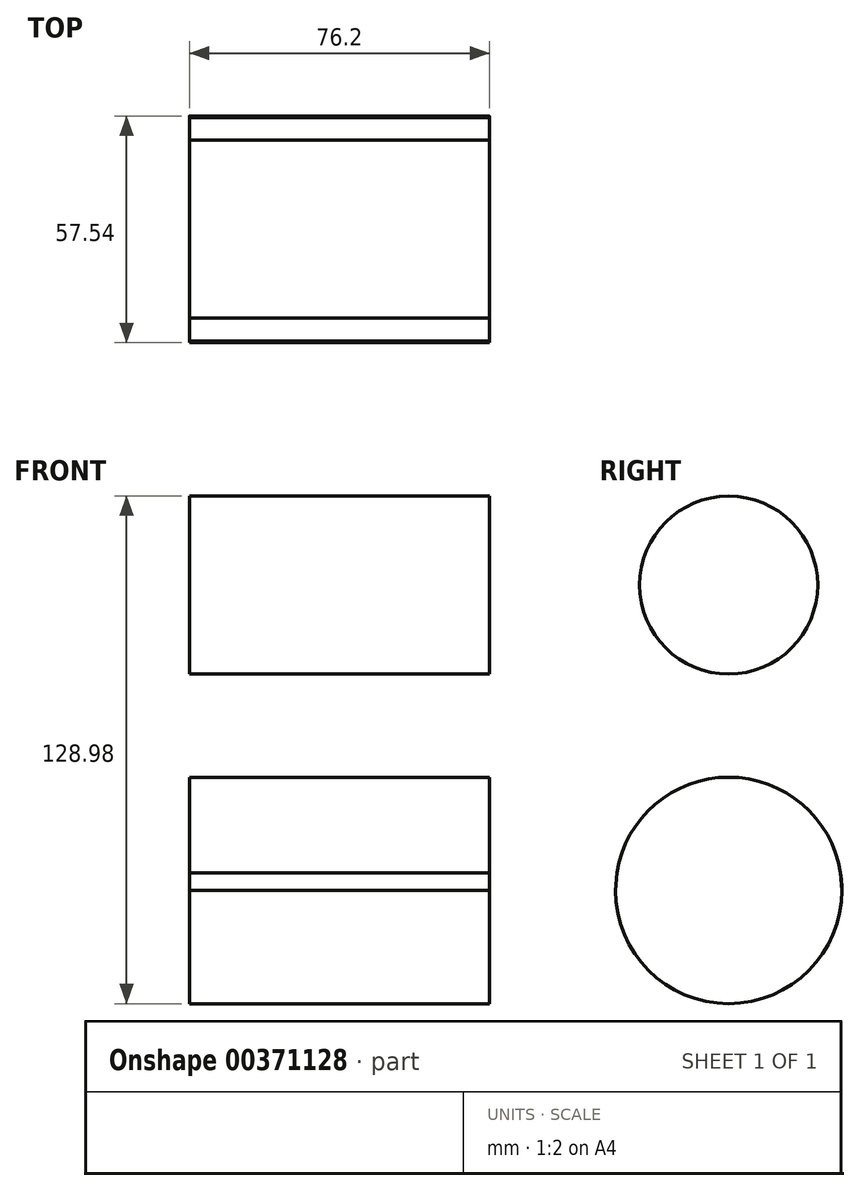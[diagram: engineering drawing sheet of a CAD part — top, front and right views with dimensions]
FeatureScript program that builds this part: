
annotation { "Feature Type Name" : "Feature", "Feature Type Description" : "" }
export const myFeature = defineFeature(function(context is Context, id is Id, definition is map)
    precondition{}
    {
        {
            var Q0;
            Q0=qCreatedBy(makeId("Right.planeOp"),FACE);
            var sketch = newSketch(context, id + "F0", { "sketchPlane" : qUnion([Q0])});
            skCircle(sketch, "E0", {"center": v(0, 0) * mm, "radius": 28.77 * mm});
            skCircle(sketch, "E1", {"center": v(0, 77.59) * mm, "radius": 22.62 * mm});
            skLineSegment(sketch, "E2", {"start": v(-28.77, 0) * mm, "end": v(-22.55, 79.36) * mm});
            skLineSegment(sketch, "E3", {"start": v(28.77, 0) * mm, "end": v(22.55, 79.36) * mm});
            skSolve(sketch);
        }
        {
            var Q0;
            {var subQ0=sQuery(id+"F0.wireOp",EDGE,"E2");var subQ1=sQuery(id+"F0.wireOp",EDGE,"E0");var subQ2=makeQuery(id+"F0.imprint","INTERSECT",VERTEX,{"disambiguationData":[OD(0.0)],"derivedFrom":[subQ1,subQ0]});Q0=makeQuery(id+"F0.imprint","IMPRINT",FACE,{"disambiguationData":[TD([[makeQuery(id+"F0.imprint","IMPRINT",EDGE,{"disambiguationData":[TD([[subQ2,1.0]])],"derivedFrom":subQ1}),1.0]])]});}
            var Q1;
            {var subQ0=sQuery(id+"F0.wireOp",EDGE,"E3");var subQ1=sQuery(id+"F0.wireOp",EDGE,"E0");var subQ2=makeQuery(id+"F0.imprint","INTERSECT",VERTEX,{"disambiguationData":[OD(0.0)],"derivedFrom":[subQ1,subQ0]});Q1=makeQuery(id+"F0.imprint","IMPRINT",FACE,{"disambiguationData":[TD([[makeQuery(id+"F0.imprint","IMPRINT",EDGE,{"disambiguationData":[TD([[subQ2,-1.0]])],"derivedFrom":subQ1}),1.0]])]});}
            var Q2;
            {var subQ0=sQuery(id+"F0.wireOp",EDGE,"E3");var subQ1=sQuery(id+"F0.wireOp",EDGE,"E0");var subQ2=makeQuery(id+"F0.imprint","INTERSECT",VERTEX,{"disambiguationData":[OD(1.0)],"derivedFrom":[subQ1,subQ0]});Q2=makeQuery(id+"F0.imprint","IMPRINT",FACE,{"disambiguationData":[TD([[makeQuery(id+"F0.imprint","IMPRINT",EDGE,{"disambiguationData":[TD([[subQ2,-1.0]])],"derivedFrom":subQ1}),-1.0]])]});}
            var Q3;
            Q3=sQuery(id+"F0.wireOp",EDGE,"E2");
            extrude(context, id + "F1", {"entities" : qUnion([Q0, Q1, Q2]), "surfaceEntities" : qUnion([Q3]), "endBound" : BoundingType.SYMMETRIC, "depth" : 76.2 * mm});
        }
        {
            var Q0;
            Q0 = qSketchRegion(id + "F0", true);
            var Q1;
            Q1=sQuery(id+"F0.wireOp",EDGE,"E1");
            var Q2;
            Q2=sQuery(id+"F0.wireOp",EDGE,"E0");
            extrude(context, id + "F2", {"entities" : qUnion([Q0]), "bodyType" : ToolBodyType.SURFACE, "surfaceEntities" : qUnion([Q1, Q2]), "endBound" : BoundingType.SYMMETRIC, "depth" : 152.4 * mm});
        }
        {
            var Q0;
            {var subQ0=sQuery(id+"F0.wireOp",EDGE,"E1");var subQ1=makeQuery(id+"F0.imprint","INTERSECT",VERTEX,{"derivedFrom":[subQ0,sQuery(id+"F0.wireOp",EDGE,"E2")]});Q0=makeQuery(id+"F0.imprint","IMPRINT",FACE,{"disambiguationData":[TD([[makeQuery(id+"F0.imprint","IMPRINT",EDGE,{"disambiguationData":[TD([[subQ1,1.0]])],"derivedFrom":subQ0}),1.0]])]});}
            var Q1;
            {var subQ0=sQuery(id+"F0.wireOp",EDGE,"E3");var subQ1=sQuery(id+"F0.wireOp",EDGE,"E0");var subQ2=makeQuery(id+"F0.imprint","INTERSECT",VERTEX,{"disambiguationData":[OD(1.0)],"derivedFrom":[subQ1,subQ0]});Q1=makeQuery(id+"F0.imprint","IMPRINT",FACE,{"disambiguationData":[TD([[makeQuery(id+"F0.imprint","IMPRINT",EDGE,{"disambiguationData":[TD([[subQ2,-1.0]])],"derivedFrom":subQ1}),1.0]])]});}
            extrude(context, id + "F3", {"entities" : qUnion([Q0, Q1]), "endBound" : BoundingType.SYMMETRIC, "depth" : 76.2 * mm});
        }
    });
